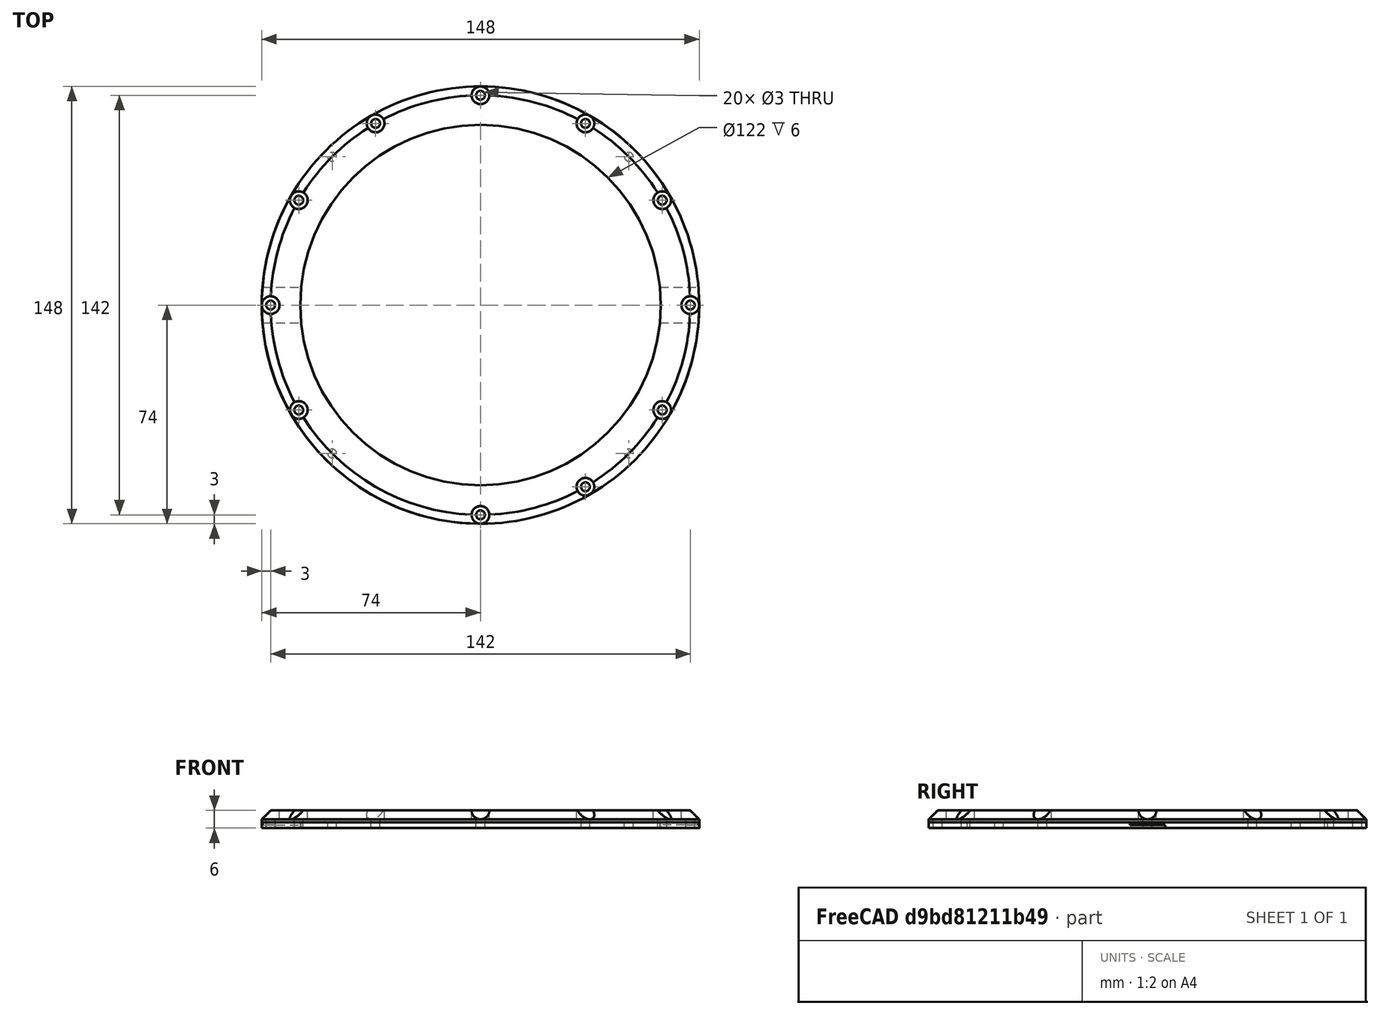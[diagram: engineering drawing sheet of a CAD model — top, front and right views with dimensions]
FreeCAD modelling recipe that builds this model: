
FCSTD DOCUMENT  (FreeCAD 0.19R24276 (Git))
Label: bazovina-part-G_seal_006
License: All rights reserved
LicenseURL: http://en.wikipedia.org/wiki/All_rights_reserved
objects: Part::Cylinder×36, Part::Cut×6, Part::Compound×4, Part::Box×4, Part::FeaturePython×3, Part::MultiFuse×1, Part::Common×1, Part::Chamfer×1, Mesh::Feature×1
note: 56 computed .brp shape members not serialized (recipe doc carries the construction recipe); baked Part::Feature solids carry a one-line shape summary decoded from their .brp

FEATURE [Part::Cylinder] Cylinder  label="Válec"
  Angle = 360
  AttacherType = Attacher::AttachEngine3D
  Height = 60
  Placement = pos=(0,-71,0) rot=(0,0,1;0rad)
  Radius = 1.5
FEATURE [Part::FeaturePython] Tube029  # WARN: FeaturePython — macro-defined, semantics opaque (R4)
  AttacherType = Attacher::AttachEngine3D
  Height = 2
  InnerRadius = 61
  OuterRadius = 74
  Placement = pos=(0,0,14) rot=(0,0,1;0rad)
FEATURE [Part::Cylinder] Cylinder500  label="Válec500"
  Angle = 360
  AttacherType = Attacher::AttachEngine3D
  Height = 60
  Placement = pos=(-50.2046,-50.2046,0) rot=(0,0,-1;0.785398rad)
  Radius = 1.5
FEATURE [Part::Cylinder] Cylinder499  label="Válec499"
  Angle = 360
  AttacherType = Attacher::AttachEngine3D
  Height = 60
  Placement = pos=(-71,-2.8e-14,0) rot=(0,0,-1;1.5708rad)
  Radius = 1.5
FEATURE [Part::Cylinder] Cylinder495  label="Válec495"
  Angle = 360
  AttacherType = Attacher::AttachEngine3D
  Height = 60
  Placement = pos=(71,5e-15,0) rot=(0,0,1;1.5708rad)
  Radius = 1.5
FEATURE [Part::Cylinder] Cylinder494  label="Válec494"
  Angle = 360
  AttacherType = Attacher::AttachEngine3D
  Height = 60
  Placement = pos=(50.2046,-50.2046,0) rot=(0,0,1;0.785398rad)
  Radius = 1.5
FEATURE [Part::Cylinder] Cylinder498  label="Válec498"
  Angle = 360
  AttacherType = Attacher::AttachEngine3D
  Height = 60
  Placement = pos=(-50.2046,50.2046,0) rot=(0,0,1;3.92699rad)
  Radius = 1.5
FEATURE [Part::Cylinder] Cylinder496  label="Válec496"
  Angle = 360
  AttacherType = Attacher::AttachEngine3D
  Height = 60
  Placement = pos=(50.2046,50.2046,0) rot=(0,0,1;2.35619rad)
  Radius = 1.5
FEATURE [Part::Compound] Compound330
  Links = -> [Cylinder,Cylinder494,Cylinder495,Cylinder496,Cylinder498,Cylinder499,Cylinder500]
FEATURE [Part::Cylinder] Cylinder501  label="Válec501"
  Angle = 360
  AttacherType = Attacher::AttachEngine3D
  Height = 60
  Placement = pos=(-50.2046,-50.2046,0) rot=(0,0,-1;0.785398rad)
  Radius = 1.5
FEATURE [Part::Cylinder] Cylinder502  label="Válec502"
  Angle = 360
  AttacherType = Attacher::AttachEngine3D
  Height = 60
  Placement = pos=(-71,-2.8e-14,0) rot=(0,0,-1;1.5708rad)
  Radius = 1.5
FEATURE [Part::Cylinder] Cylinder503  label="Válec503"
  Angle = 360
  AttacherType = Attacher::AttachEngine3D
  Height = 60
  Placement = pos=(0,-71,0) rot=(0,0,1;0rad)
  Radius = 1.5
FEATURE [Part::FeaturePython] Tube030  # WARN: FeaturePython — macro-defined, semantics opaque (R4)
  AttacherType = Attacher::AttachEngine3D
  Height = 2
  InnerRadius = 61
  OuterRadius = 74
  Placement = pos=(0,0,14) rot=(0,0,1;0rad)
FEATURE [Part::Cylinder] Cylinder504  label="Válec504"
  Angle = 360
  AttacherType = Attacher::AttachEngine3D
  Height = 60
  Placement = pos=(71,5e-15,0) rot=(0,0,1;1.5708rad)
  Radius = 1.5
FEATURE [Part::Cylinder] Cylinder505  label="Válec505"
  Angle = 360
  AttacherType = Attacher::AttachEngine3D
  Height = 60
  Placement = pos=(50.2046,-50.2046,0) rot=(0,0,1;0.785398rad)
  Radius = 1.5
FEATURE [Part::Cylinder] Cylinder506  label="Válec506"
  Angle = 360
  AttacherType = Attacher::AttachEngine3D
  Height = 60
  Placement = pos=(-50.2046,50.2046,0) rot=(0,0,1;3.92699rad)
  Radius = 1.5
FEATURE [Part::Cylinder] Cylinder507  label="Válec507"
  Angle = 360
  AttacherType = Attacher::AttachEngine3D
  Height = 60
  Placement = pos=(50.2046,50.2046,0) rot=(0,0,1;2.35619rad)
  Radius = 1.5
FEATURE [Part::Compound] Compound331
  Links = -> [Cylinder503,Cylinder505,Cylinder504,Cylinder507,Cylinder506,Cylinder502,Cylinder501]
FEATURE [Part::Cut] Cut205  label="bazovina-part-G001"
  Base = -> Tube030
  Tool = -> Compound331
FEATURE [Part::Box] Box  label="Krychle"
  AttacherType = Attacher::AttachEngine3D
  Height = 1
  Length = 180
  Placement = pos=(-90,-174,14) rot=(0,0,1;0rad)
  Width = 180
FEATURE [Part::Box] Box001  label="Krychle001"
  AttacherType = Attacher::AttachEngine3D
  Height = 2
  Length = 180
  Placement = pos=(-90,-186,14) rot=(0,0,1;0rad)
  Width = 180
FEATURE [Part::Box] Box002  label="Krychle002"
  AttacherType = Attacher::AttachEngine3D
  Height = 2
  Length = 180
  Placement = pos=(-90,-186,14) rot=(0,0,1;0rad)
  Width = 180
FEATURE [Part::Box] Box003  label="Krychle003"
  AttacherType = Attacher::AttachEngine3D
  Height = 1
  Length = 180
  Placement = pos=(-90,-174,14) rot=(0,0,1;0rad)
  Width = 180
FEATURE [Part::Cut] Cut204  label="bazovina-part-G"
  Base = -> Tube029
  Tool = -> Compound330
FEATURE [Part::Cut] Cut
  Base = -> Cut204
  Tool = -> Box
FEATURE [Part::Cut] Cut206  label="bazovina-part-G1"
  Base = -> Cut
  Tool = -> Box001
FEATURE [Part::MultiFuse] Fusion
  Shapes = -> [Box003,Box002]
FEATURE [Part::Common] Common  label="bazovina-part-G2"
  Base = -> Cut205
  Tool = -> Fusion
FEATURE [Part::Cylinder] Cylinder978  label="Válec978"
  Angle = 360
  AttacherType = Attacher::AttachEngine3D
  Height = 60
  Placement = pos=(35.5,61.4878,0) rot=(0,0,1;2.61799rad)
  Radius = 1.5
FEATURE [Part::Cylinder] Cylinder981  label="Válec981"
  Angle = 360
  AttacherType = Attacher::AttachEngine3D
  Height = 60
  Placement = pos=(-61.4878,35.5,0) rot=(0,0,1;4.18879rad)
  Radius = 1.5
FEATURE [Part::Cylinder] Cylinder983  label="Válec983"
  Angle = 360
  AttacherType = Attacher::AttachEngine3D
  Height = 60
  Placement = pos=(-61.4878,-35.5,0) rot=(0,0,-1;1.0472rad)
  Radius = 1.5
FEATURE [Part::Cylinder] Cylinder976  label="Válec976"
  Angle = 360
  AttacherType = Attacher::AttachEngine3D
  Height = 60
  Placement = pos=(71,-1.8e-14,0) rot=(0,0,1;1.5708rad)
  Radius = 1.5
FEATURE [Part::Cylinder] Cylinder977  label="Válec977"
  Angle = 360
  AttacherType = Attacher::AttachEngine3D
  Height = 60
  Placement = pos=(61.4878,35.5,0) rot=(0,0,1;2.0944rad)
  Radius = 1.5
FEATURE [Part::Cylinder] Cylinder979  label="Válec979"
  Angle = 360
  AttacherType = Attacher::AttachEngine3D
  Height = 60
  Placement = pos=(3.1e-14,71,0) rot=(0,0,1;3.14159rad)
  Radius = 1.5
FEATURE [Part::Cylinder] Cylinder982  label="Válec982"
  Angle = 360
  AttacherType = Attacher::AttachEngine3D
  Height = 60
  Placement = pos=(-71,2.7e-14,0) rot=(0,0,-1;1.5708rad)
  Radius = 1.5
FEATURE [Part::Cylinder] Cylinder975  label="Válec975"
  Angle = 360
  AttacherType = Attacher::AttachEngine3D
  Height = 60
  Placement = pos=(61.4878,-35.5,0) rot=(0,0,1;1.0472rad)
  Radius = 1.5
FEATURE [Part::Cylinder] Cylinder973  label="Válec973"
  Angle = 360
  AttacherType = Attacher::AttachEngine3D
  Height = 60
  Placement = pos=(0,-71,0) rot=(0,0,1;0rad)
  Radius = 1.5
FEATURE [Part::Cylinder] Cylinder974  label="Válec974"
  Angle = 360
  AttacherType = Attacher::AttachEngine3D
  Height = 60
  Placement = pos=(35.5,-61.4878,0) rot=(0,0,1;0.523599rad)
  Radius = 1.5
FEATURE [Part::Cylinder] Cylinder980  label="Válec980"
  Angle = 360
  AttacherType = Attacher::AttachEngine3D
  Height = 60
  Placement = pos=(-35.5,61.4878,0) rot=(0,0,1;3.66519rad)
  Radius = 1.5
FEATURE [Part::Compound] Compound525
  Links = -> [Cylinder973,Cylinder974,Cylinder975,Cylinder976,Cylinder977,Cylinder978,Cylinder979,Cylinder980,Cylinder981,Cylinder982,Cylinder983]
FEATURE [Part::FeaturePython] Tube031  # WARN: FeaturePython — macro-defined, semantics opaque (R4)
  AttacherType = Attacher::AttachEngine3D
  Height = 6
  InnerRadius = 61
  OuterRadius = 74
  Placement = pos=(0,0,14) rot=(0,0,1;0rad)
FEATURE [Part::Cylinder] Cylinder984  label="Válec984"
  Angle = 360
  AttacherType = Attacher::AttachEngine3D
  Height = 3
  Placement = pos=(35.5,61.4878,0) rot=(0,0,1;2.61799rad)
  Radius = 3
FEATURE [Part::Cylinder] Cylinder985  label="Válec985"
  Angle = 360
  AttacherType = Attacher::AttachEngine3D
  Height = 3
  Placement = pos=(-61.4878,35.5,0) rot=(0,0,1;4.18879rad)
  Radius = 3
FEATURE [Part::Cylinder] Cylinder986  label="Válec986"
  Angle = 360
  AttacherType = Attacher::AttachEngine3D
  Height = 3
  Placement = pos=(-71,2.7e-14,0) rot=(0,0,-1;1.5708rad)
  Radius = 3
FEATURE [Part::Cylinder] Cylinder987  label="Válec987"
  Angle = 360
  AttacherType = Attacher::AttachEngine3D
  Height = 3
  Placement = pos=(71,-1.8e-14,0) rot=(0,0,1;1.5708rad)
  Radius = 3
FEATURE [Part::Cylinder] Cylinder988  label="Válec988"
  Angle = 360
  AttacherType = Attacher::AttachEngine3D
  Height = 3
  Placement = pos=(61.4878,35.5,0) rot=(0,0,1;2.0944rad)
  Radius = 3
FEATURE [Part::Cylinder] Cylinder989  label="Válec989"
  Angle = 360
  AttacherType = Attacher::AttachEngine3D
  Height = 3
  Placement = pos=(3.1e-14,71,0) rot=(0,0,1;3.14159rad)
  Radius = 3
FEATURE [Part::Cylinder] Cylinder990  label="Válec990"
  Angle = 360
  AttacherType = Attacher::AttachEngine3D
  Height = 3
  Placement = pos=(35.5,-61.4878,0) rot=(0,0,1;0.523599rad)
  Radius = 3
FEATURE [Part::Cylinder] Cylinder991  label="Válec991"
  Angle = 360
  AttacherType = Attacher::AttachEngine3D
  Height = 3
  Placement = pos=(61.4878,-35.5,0) rot=(0,0,1;1.0472rad)
  Radius = 3
FEATURE [Part::Cylinder] Cylinder992  label="Válec992"
  Angle = 360
  AttacherType = Attacher::AttachEngine3D
  Height = 3
  Placement = pos=(-61.4878,-35.5,0) rot=(0,0,-1;1.0472rad)
  Radius = 3
FEATURE [Part::Cylinder] Cylinder993  label="Válec993"
  Angle = 360
  AttacherType = Attacher::AttachEngine3D
  Height = 3
  Placement = pos=(0,-71,0) rot=(0,0,1;0rad)
  Radius = 3
FEATURE [Part::Cylinder] Cylinder994  label="Válec994"
  Angle = 360
  AttacherType = Attacher::AttachEngine3D
  Height = 3
  Placement = pos=(-35.5,61.4878,0) rot=(0,0,1;3.66519rad)
  Radius = 3
FEATURE [Part::Compound] Compound526
  Links = -> [Cylinder993,Cylinder990,Cylinder991,Cylinder987,Cylinder988,Cylinder984,Cylinder989,Cylinder994,Cylinder985,Cylinder986,Cylinder992]
  Placement = pos=(0,0,17) rot=(0,0,1;0rad)
FEATURE [Part::Chamfer] Chamfer
  Base = -> Tube031
  Edges = 1 edges r=3: [Edge1]
FEATURE [Part::Cut] Cut207
  Base = -> Chamfer
  Tool = -> Compound526
FEATURE [Part::Cut] Cut208  label="bazovina_part-G_seal"
  Base = -> Cut207
  Tool = -> Compound525
FEATURE [Mesh::Feature] Mesh  label="bazovina_part-G_seal (Meshed)"
